# Revit family: 6218_Gewindetülle mit Konus
name_source: partatom
category: Rohrformteile
units: mm (PartAtom-declared; Revit-internal decimal feet)

## family parameters
Arbeitsebenenbasiert = Nein
Beim Laden mit Abzugskörper schneiden = Nein
Bemaßung runder Anschluss = Durchmesser verwenden
Gemeinsam genutzt = Nein
Immer vertikal = Ja
OmniClass-Nummer = 23.65.55.14
OmniClass-Titel = Valves for Liquid Services
Teiletyp = Verbindung

## types (5) — shared parameters
Ausführung = Gewindetülle, ohne Mutter, mit Konus, zum ausgleichen von Baumaßdifferenzen
D00 = 12 mm  [stored 0.0393701 ft]
D01 = 11 mm
D02 = 9 mm  [stored 0.0295276 ft]
D03 = 11 mm
D04 = 8 mm  [stored 0.0262467 ft]
Gewindetülle = Messing CW614N, vernickelt
Hersteller = HERZ Armaturen Ges.m.b.H.
Hinweiß = Der O-Ring dient als zusätzliche Dichtung, bei Verlust ist die Gewindetülle metallisch dichtend.
L01 = 8 mm  [stored 0.0262467 ft]
L02 = 3 mm  [stored 0.00984252 ft]
L03 = 13 mm
Max. Betriebsdruck = 1000000.0 Pa
Max. Betriebstemperatur = 110 °C
Medium = Heizungswasser nach ÖNORM H5195 oder VDI- Richtlinie 2035.
Die Verwendung von Ethylen- oder Propyleneglykol in einem Mischungsverhältnis 25- 50% ist zulässig.
Nennweite = 15 mm  [stored 0.0492126 ft]
O-Ring = EPDM
R01 = 11 mm
SCRNCODE = 07;01;01
SCRNSEQ = AWI;AWI_TYP="1001";1
URL = www.herz-armaturen.at
zero-valued in all types: Vorgabe-Ansicht

## per-type parameters (varying)
| type | 1_2x36 | 1_2x39 | 1_2x42 | 1_2x48 | 1_2x76 | L00 |
| R1/2x39mm | Nein | Ja | Nein | Nein | Nein | 39 mm |
| R1/2x36mm | Ja | Nein | Nein | Nein | Nein | 36 mm |
| R1/2x42mm | Nein | Nein | Ja | Nein | Nein | 42 mm |
| R1/2x48mm | Nein | Nein | Nein | Ja | Nein | 48 mm |
| R1/2x76mm | Nein | Nein | Nein | Nein | Ja | 76 mm  [stored 0.249344 ft] |

note: [stored X ft] marks values corroborated as IEEE doubles in the binary element streams (Revit-internal decimal feet)
